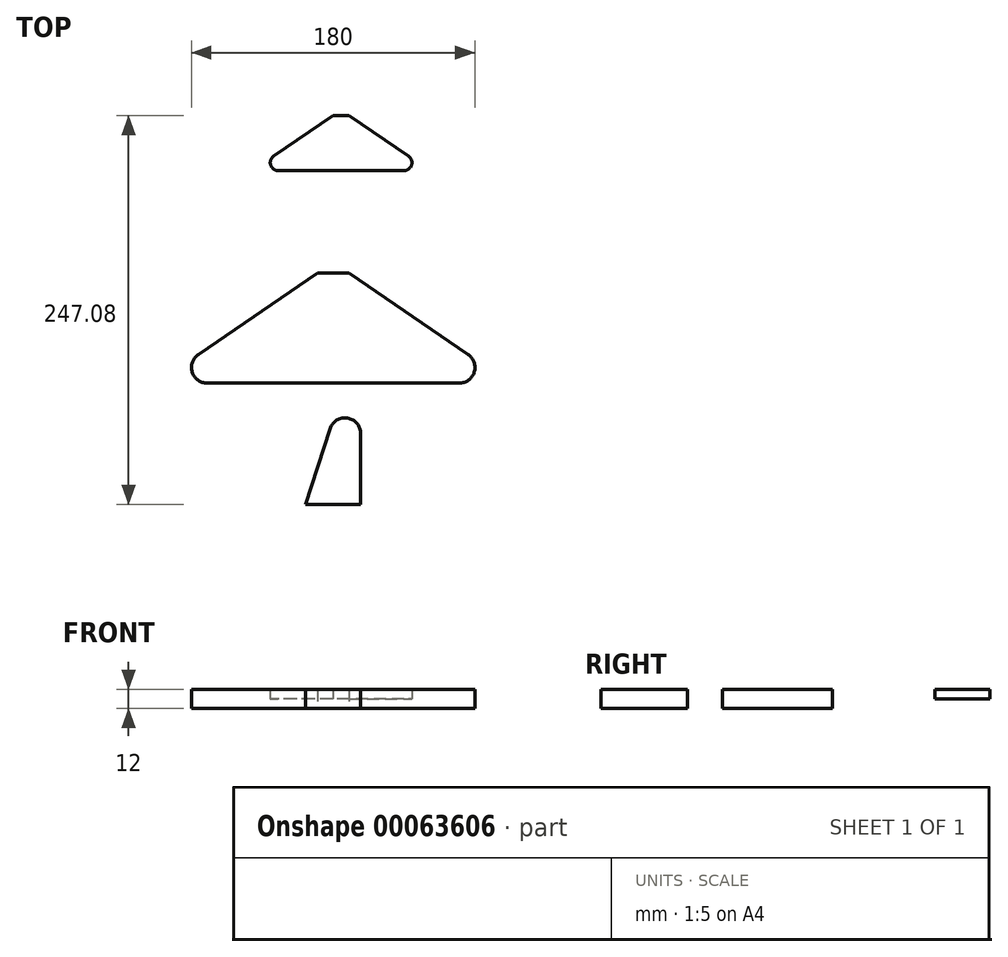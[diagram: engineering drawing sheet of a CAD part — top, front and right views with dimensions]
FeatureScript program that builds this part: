
annotation { "Feature Type Name" : "Feature", "Feature Type Description" : "" }
export const myFeature = defineFeature(function(context is Context, id is Id, definition is map)
    precondition{}
    {
        {
            var Q0;
            Q0=qCreatedBy(makeId("Top.planeOp"),FACE);
            var sketch = newSketch(context, id + "F0", { "sketchPlane" : qUnion([Q0])});
            skLineSegment(sketch, "E0.bottom", {"start": v(10, 35) * mm, "end": v(-10, 35) * mm});
            skLineSegment(sketch, "E0.top", {"start": v(80, -35) * mm, "end": v(-80, -35) * mm});
            skPoint(sketch, "E0.middle", {"position": v(0, 0) * mm});
            skLineSegment(sketch, "E1", {"start": v(-10, 44.03) * mm, "end": v(-10, -52.06) * mm, "construction": true});
            skLineSegment(sketch, "E2", {"start": v(10, 44.55) * mm, "end": v(10, -55.68) * mm, "construction": true});
            skArc(sketch, "E3", {"start": v(-85.65, -16.75) * mm, "mid": v(-89.55, -27.95) * mm, "end": v(-80, -35) * mm});
            skArc(sketch, "E4", {"start": v(80, -35) * mm, "mid": v(89.55, -27.95) * mm, "end": v(85.65, -16.75) * mm});
            skLineSegment(sketch, "E5", {"start": v(10, 35) * mm, "end": v(85.65, -16.75) * mm});
            skLineSegment(sketch, "E6", {"start": v(-10, 35) * mm, "end": v(-85.65, -16.75) * mm});
            skPoint(sketch, "E7.orphan", {"position": v(-90, 35) * mm});
            skPoint(sketch, "E8.orphan", {"position": v(-90, -35) * mm});
            skPoint(sketch, "E9.orphan", {"position": v(90, 35) * mm});
            skPoint(sketch, "E10.orphan", {"position": v(90, -35) * mm});
            skSolve(sketch);
        }
        {
            var Q0;
            Q0=makeQuery(id+"F0.imprint","IMPRINT",FACE,{"disambiguationData":[TD([[makeQuery(id+"F0.imprint","IMPRINT",EDGE,{"derivedFrom":sQuery(id+"F0.wireOp",EDGE,"E0.bottom")}),1.0]])]});
            extrude(context, id + "F1", {"entities" : qUnion([Q0]), "depth" : 12 * mm});
        }
        {
            var Q0;
            Q0=makeQuery(id+"F1.opExtrude","SWEPT_BODY",BODY,{"disambiguationData":[OSD([sQuery(id+"F0.wireOp",EDGE,"E0.bottom"),sQuery(id+"F0.wireOp",EDGE,"E0.top"),sQuery(id+"F0.wireOp",EDGE,"E3"),sQuery(id+"F0.wireOp",EDGE,"E4"),sQuery(id+"F0.wireOp",EDGE,"E5"),sQuery(id+"F0.wireOp",EDGE,"E6")])]});
            transform(context, id + "F2", {"entities" : qUnion([Q0]), "transformType" : TransformType.TRANSLATION_3D, "dx" : 0 * mm, "dy" : 100 * mm, "dz" : 0 * mm, "makeCopy" : true});
        }
        {
            var Q0;
            Q0=makeQuery(id+"F2.opPattern","COPY",BODY,{"derivedFrom":makeQuery(id+"F1.opExtrude","SWEPT_BODY",BODY,{"disambiguationData":[OSD([sQuery(id+"F0.wireOp",EDGE,"E0.bottom"),sQuery(id+"F0.wireOp",EDGE,"E0.top"),sQuery(id+"F0.wireOp",EDGE,"E3"),sQuery(id+"F0.wireOp",EDGE,"E4"),sQuery(id+"F0.wireOp",EDGE,"E5"),sQuery(id+"F0.wireOp",EDGE,"E6")])]}),"instanceName":"1"});
            var Q1;
            Q1=makeQuery(id+"F2.opPattern","COPY",VERTEX,{"derivedFrom":makeQuery(id+"F1.opExtrude","CAP_VERTEX",VERTEX,{"disambiguationData":[OSD([sQuery(id+"F0.wireOp",EDGE,"E0.bottom"),sQuery(id+"F0.wireOp",EDGE,"E5")])],"isStart":false}),"instanceName":"1"});
            transform(context, id + "F3", {"entities" : qUnion([Q0]), "transformType" : TransformType.SCALE_UNIFORMLY, "scale" : 0.5, "scalePoint" : qUnion([Q1]), "makeCopy" : false});
        }
        {
            var Q0;
            Q0=qCreatedBy(makeId("Top.planeOp"),FACE);
            var sketch = newSketch(context, id + "F4", { "sketchPlane" : qUnion([Q0])});
            skLineSegment(sketch, "E11.bottom", {"start": v(17.5, -112.08) * mm, "end": v(-17.5, -112.08) * mm});
            skLineSegment(sketch, "E11.left", {"start": v(17.5, -112.08) * mm, "end": v(17.5, -67.08) * mm});
            skPoint(sketch, "E11.middle", {"position": v(0, -84.58) * mm});
            skLineSegment(sketch, "E12", {"start": v(22.17, -67.08) * mm, "end": v(-10.14, -67.08) * mm, "construction": true});
            skLineSegment(sketch, "E13", {"start": v(7.5, -51.36) * mm, "end": v(7.5, -76.24) * mm, "construction": true});
            skArc(sketch, "E14", {"start": v(17.5, -67.08) * mm, "mid": v(9.05, -57.2) * mm, "end": v(-2.02, -64.01) * mm});
            skLineSegment(sketch, "E15", {"start": v(-17.5, -112.08) * mm, "end": v(-2.02, -64.01) * mm});
            skPoint(sketch, "E16.orphan", {"position": v(17.5, -57.08) * mm});
            skPoint(sketch, "E11.right.end.orphan", {"position": v(-17.5, -57.08) * mm});
            skSolve(sketch);
        }
        {
            var Q0;
            Q0 = qSketchRegion(id + "F4", true);
            var Q1;
            Q1=makeQuery(id+"F4.imprint","IMPRINT",FACE,{"disambiguationData":[TD([[makeQuery(id+"F4.imprint","IMPRINT",EDGE,{"derivedFrom":sQuery(id+"F4.wireOp",EDGE,"E11.bottom")}),-1.0]])]});
            extrude(context, id + "F5", {"entities" : qUnion([Q0, Q1]), "depth" : 12 * mm});
        }
    });
